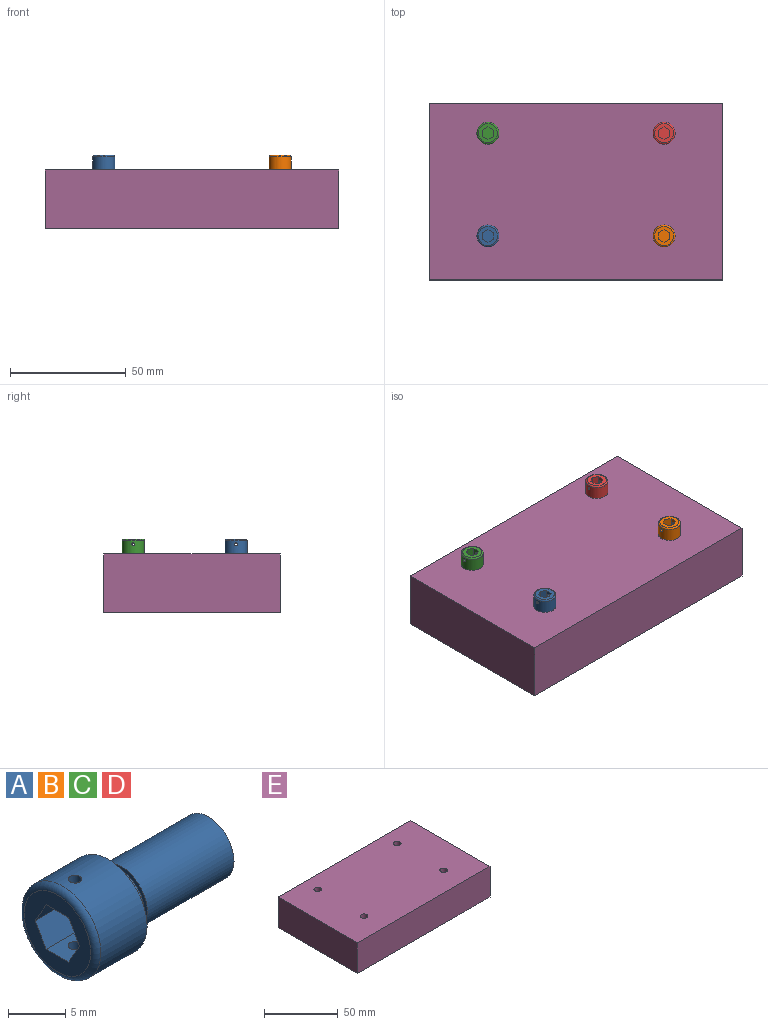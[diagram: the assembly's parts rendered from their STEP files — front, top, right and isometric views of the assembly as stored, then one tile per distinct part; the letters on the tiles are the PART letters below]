
ASSEMBLY  parts=5 mates=1
PART A: 19 faces, bbox 19.1x10.3x10.3 mm
  f0: cylinder r=3.17mm len=6.35mm, axis (1,0,0), area 25.3mm2, adj f4,f18
  f1: torus R=4.13mm, axis (1,0,0), area 28.4mm2, adj f5,f17
  f2: cone r=2.83mm half-angle=63.4deg, axis (-1,0,0), area 13.6mm2, adj f3,f16
  f3: cylinder r=3.17mm len=10.74mm, axis (1,0,0), area 214.3mm2, adj f2,f15
  f4: cone r=2.83mm half-angle=63.4deg, axis (-1,0,0), area 13.6mm2, adj f0,f15
  f5: cylinder r=4.76mm len=9.53mm, axis (1,0,0), area 168.8mm2, adj f1,f6,f7,f18
  f6: cylinder r=0.59mm len=2.38mm, axis (0,0,1), area 8.8mm2, adj f5,f10
  f7: cylinder r=0.59mm len=2.38mm, axis (0,0,1), area 8.8mm2, adj f5,f12
  f8: plane 3.81x2.39mm, normal (0,-0.87,0.5), area 10.5mm2, adj f9,f12,f14,f17
  f9: plane 3.81x2.39mm, normal (0,-0.87,-0.5), area 10.5mm2, adj f8,f10,f14,f17
  f10: plane 3.81x2.76mm, normal (0,0,-1), area 9.4mm2, adj f6,f9,f11,f14,f17
  f11: plane 3.81x2.39mm, normal (0,0.87,-0.5), area 10.5mm2, adj f10,f13,f14,f17
  f12: plane 3.81x2.76mm, normal (0,0,1), area 9.4mm2, adj f7,f8,f13,f14,f17
  f13: plane 3.81x2.39mm, normal (0,0.87,0.5), area 10.5mm2, adj f11,f12,f14,f17
  f14: plane 5.51x4.78mm, normal (-1,0,0), area 19.7mm2, adj f8,f9,f10,f11,f12,f13
  f15: plane 6.35x6.35mm, normal (-1,0,0), area 12.2mm2, adj f3,f4
  f16: plane 4.98x4.98mm, normal (1,0,0), area 19.5mm2, adj f2
  f17: plane 8.26x8.26mm, normal (-1,0,0), area 33.8mm2, adj f1,f8,f9,f10,f11,f12,f13
  f18: plane 9.53x9.53mm, normal (1,0,0), area 39.6mm2, adj f0,f5
PART B: same geometry as A
PART C: same geometry as A
PART D: same geometry as A
PART E: 10 faces, bbox 127x76.2x25.4 mm
  f0: plane 76.2x25.4mm, normal (1,0,0), area 1935.5mm2, adj f1,f3,f4,f5
  f1: plane 127x25.4mm, normal (0,1,0), area 3225.8mm2, adj f0,f2,f4,f5
  f2: plane 76.2x25.4mm, normal (-1,0,0), area 1935.5mm2, adj f1,f3,f4,f5
  f3: plane 127x25.4mm, normal (0,-1,0), area 3225.8mm2, adj f0,f2,f4,f5
  f4: plane 127x76.2mm, normal (0,0,1), area 9595.5mm2, adj f0,f1,f2,f3,f6,f7,f8,f9
  f5: plane 127x76.2mm, normal (0,0,-1), area 9595.5mm2, adj f0,f1,f2,f3,f6,f7,f8,f9
  f6: cylinder r=2.55mm len=25.4mm, axis (0,0,1), area 407.4mm2, adj f4,f5
  f7: cylinder r=2.55mm len=25.4mm, axis (0,0,1), area 407.4mm2, adj f4,f5
  f8: cylinder r=2.55mm len=25.4mm, axis (0,0,1), area 407.4mm2, adj f4,f5
  f9: cylinder r=2.55mm len=25.4mm, axis (0,0,1), area 407.4mm2, adj f4,f5
PLACE A rot(axis=(0.71,0,-0.71),180deg) t=(-34.23,-16.1,13.77)mm
PLACE B rot(axis=(0.71,0,-0.71),180deg) t=(41.97,-16.1,13.77)mm
PLACE C rot(axis=(0.71,0,-0.71),180deg) t=(-34.23,28.35,13.77)mm
PLACE D rot(axis=(0.71,0,-0.71),180deg) t=(41.97,28.35,13.77)mm
PLACE E t=(3.87,2.95,-11.63)mm fixed
MATE cylindrical A.f0 <-> E.f7  axis (0,0,-1) through (-34.23,-16.1,13.77)mm
